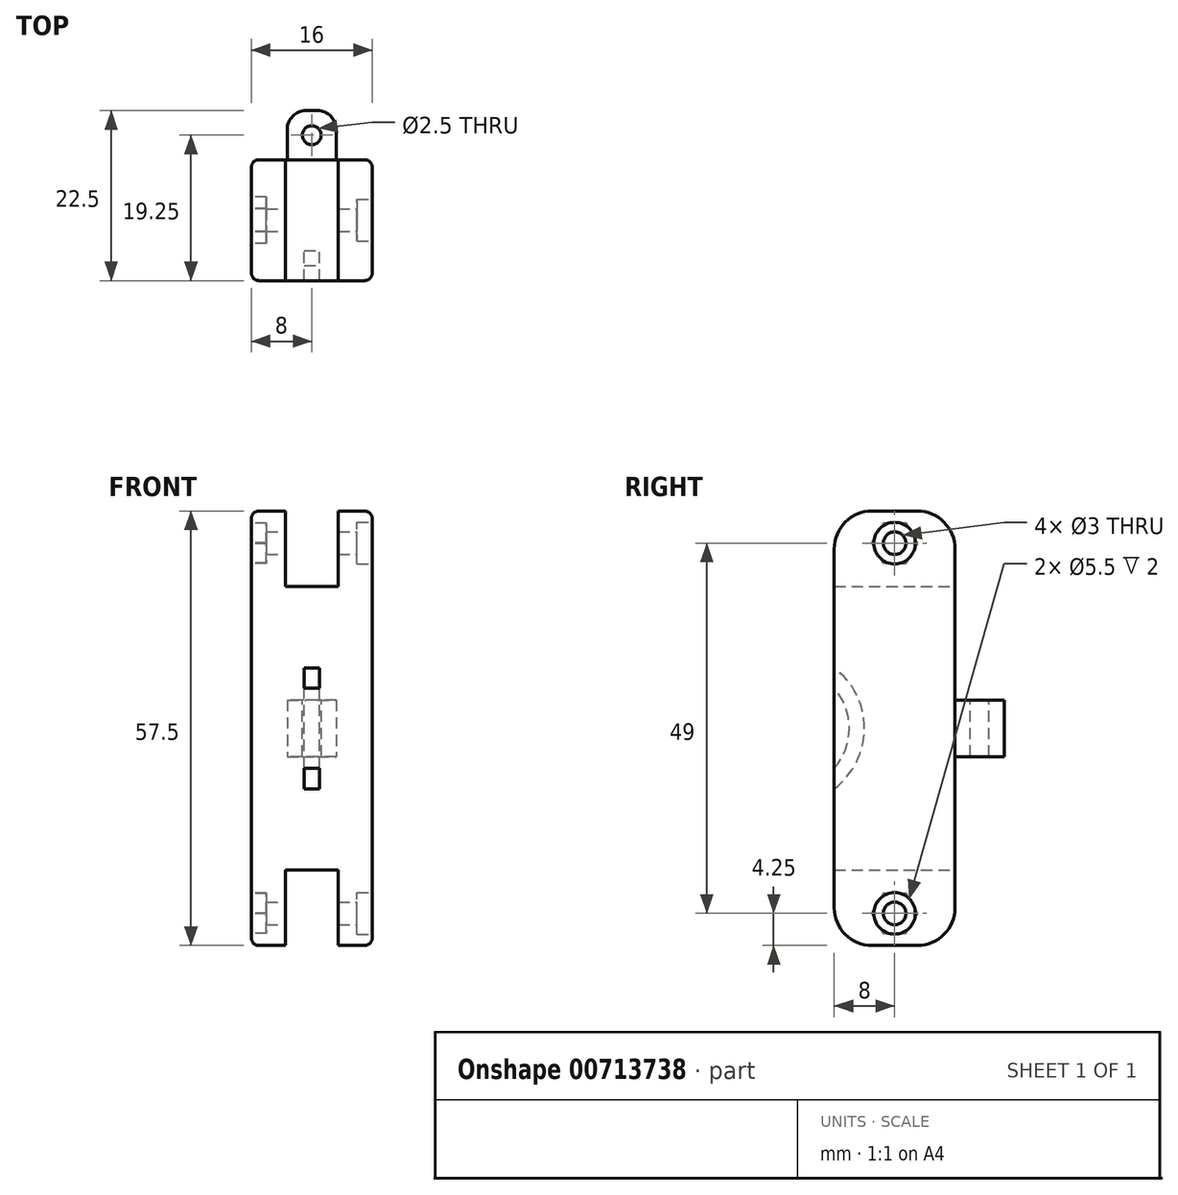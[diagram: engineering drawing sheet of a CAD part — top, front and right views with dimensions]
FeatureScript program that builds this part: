
annotation { "Feature Type Name" : "Feature", "Feature Type Description" : "" }
export const myFeature = defineFeature(function(context is Context, id is Id, definition is map)
    precondition{}
    {
        {
            var Q0;
            Q0=qCreatedBy(makeId("Front.planeOp"),FACE);
            var sketch = newSketch(context, id + "F0", { "sketchPlane" : qUnion([Q0])});
            skLineSegment(sketch, "E0.bottom", {"start": v(8, -28.75) * mm, "end": v(-8, -28.75) * mm});
            skLineSegment(sketch, "E0.top", {"start": v(8, 28.75) * mm, "end": v(-8, 28.75) * mm});
            skLineSegment(sketch, "E0.left", {"start": v(8, -28.75) * mm, "end": v(8, 28.75) * mm});
            skLineSegment(sketch, "E0.right", {"start": v(-8, -28.75) * mm, "end": v(-8, 28.75) * mm});
            skPoint(sketch, "E0.middle", {"position": v(0, 0) * mm});
            skLineSegment(sketch, "E1.top", {"start": v(-3.5, -18.75) * mm, "end": v(3.5, -18.75) * mm});
            skLineSegment(sketch, "E1.left", {"start": v(-3.5, -28.75) * mm, "end": v(-3.5, -18.75) * mm});
            skLineSegment(sketch, "E1.right", {"start": v(3.5, -28.75) * mm, "end": v(3.5, -18.75) * mm});
            skLineSegment(sketch, "E2.bottom", {"start": v(-3.5, 28.75) * mm, "end": v(3.5, 28.75) * mm});
            skLineSegment(sketch, "E2.top", {"start": v(-3.5, 18.75) * mm, "end": v(3.5, 18.75) * mm});
            skLineSegment(sketch, "E2.left", {"start": v(-3.5, 28.75) * mm, "end": v(-3.5, 18.75) * mm});
            skLineSegment(sketch, "E2.right", {"start": v(3.5, 28.75) * mm, "end": v(3.5, 18.75) * mm});
            skPoint(sketch, "E3", {"position": v(0, 23) * mm});
            skPoint(sketch, "E4", {"position": v(0, -26) * mm});
            skPoint(sketch, "E5", {"position": v(0, 18.75) * mm});
            skLineSegment(sketch, "E6", {"start": v(-3.5, -28.75) * mm, "end": v(3.5, -28.75) * mm});
            skLineSegment(sketch, "E7.bottom", {"start": v(3.25, 3.75) * mm, "end": v(-3.25, 3.75) * mm});
            skLineSegment(sketch, "E7.top", {"start": v(3.25, -3.75) * mm, "end": v(-3.25, -3.75) * mm});
            skLineSegment(sketch, "E7.left", {"start": v(3.25, 3.75) * mm, "end": v(3.25, -3.75) * mm});
            skLineSegment(sketch, "E7.right", {"start": v(-3.25, 3.75) * mm, "end": v(-3.25, -3.75) * mm});
            skSolve(sketch);
        }
        {
            var Q0;
            {var subQ1=sQuery(id+"F0.wireOp",EDGE,"E0.left");Q0=makeQuery(id+"F0.imprint","IMPRINT",FACE,{"disambiguationData":[TD([[makeQuery(id+"F0.imprint","IMPRINT",EDGE,{"derivedFrom":subQ1}),1.0]])]});}
            extrude(context, id + "F1", {"entities" : qUnion([Q0]), "endBound" : BoundingType.SYMMETRIC, "depth" : 16 * mm});
        }
        {
            var Q0;
            Q0=makeQuery(id+"F1.opExtrude","SWEPT_FACE",FACE,{"disambiguationData":[OSD([sQuery(id+"F0.wireOp",EDGE,"E0.left")])]});
            var sketch = newSketch(context, id + "F2", { "sketchPlane" : qUnion([Q0])});
            skLineSegment(sketch, "E8", {"start": v(0, 28.75) * mm, "end": v(0, 24.5) * mm});
            skPoint(sketch, "E8.endSnap0", {"position": v(0, 28.75) * mm});
            skLineSegment(sketch, "E9", {"start": v(0, -28.75) * mm, "end": v(0, -24.5) * mm});
            skPoint(sketch, "E9.endSnap0", {"position": v(0, -28.75) * mm});
            skCircle(sketch, "E10", {"center": v(0, 24.5) * mm, "radius": 2.75 * mm});
            skCircle(sketch, "E11", {"center": v(0, -24.5) * mm, "radius": 2.75 * mm});
            skCircle(sketch, "E12", {"center": v(0, 24.5) * mm, "radius": 1.5 * mm});
            skCircle(sketch, "E13", {"center": v(0, -24.5) * mm, "radius": 1.5 * mm});
            skSolve(sketch);
        }
        {
            var Q0;
            Q0=makeQuery(id+"F2.imprint","IMPRINT",FACE,{"disambiguationData":[TD([[makeQuery(id+"F2.imprint","IMPRINT",EDGE,{"derivedFrom":sQuery(id+"F2.wireOp",EDGE,"E10")}),1.0]])]});
            var Q1;
            Q1=makeQuery(id+"F2.imprint","IMPRINT",FACE,{"disambiguationData":[TD([[makeQuery(id+"F2.imprint","IMPRINT",EDGE,{"derivedFrom":sQuery(id+"F2.wireOp",EDGE,"E11")}),1.0]])]});
            extrude(context, id + "F3", {"entities" : qUnion([Q0, Q1]), "operationType" : NewBodyOperationType.REMOVE, "oppositeDirection" : true, "depth" : 2 * mm});
        }
        {
            var Q0;
            Q0=makeQuery(id+"F3.boolean.opBoolean","SPLIT",FACE,{"disambiguationData":[TD([makeQuery(id+"F3.opExtrude","SWEPT_FACE",FACE,{"disambiguationData":[OSD([sQuery(id+"F2.wireOp",EDGE,"E12")])]})])],"derivedFrom":makeQuery(id+"F1.opExtrude","SWEPT_FACE",FACE,{"disambiguationData":[OSD([sQuery(id+"F0.wireOp",EDGE,"E0.left")])]})});
            var Q1;
            Q1=makeQuery(id+"F3.boolean.opBoolean","SPLIT",FACE,{"disambiguationData":[TD([makeQuery(id+"F3.opExtrude","SWEPT_FACE",FACE,{"disambiguationData":[OSD([sQuery(id+"F2.wireOp",EDGE,"E13")])]})])],"derivedFrom":makeQuery(id+"F1.opExtrude","SWEPT_FACE",FACE,{"disambiguationData":[OSD([sQuery(id+"F0.wireOp",EDGE,"E0.left")])]})});
            extrude(context, id + "F4", {"entities" : qUnion([Q0, Q1]), "operationType" : NewBodyOperationType.REMOVE, "oppositeDirection" : true, "depth" : 25 * mm});
        }
        {
            var Q0;
            Q0=makeQuery(id+"F1.opExtrude","SWEPT_FACE",FACE,{"disambiguationData":[OSD([sQuery(id+"F0.wireOp",EDGE,"E0.right")])]});
            var sketch = newSketch(context, id + "F5", { "sketchPlane" : qUnion([Q0])});
            skLineSegment(sketch, "E14", {"start": v(0, 28.75) * mm, "end": v(0, 24.5) * mm});
            skLineSegment(sketch, "E15", {"start": v(0, -28.75) * mm, "end": v(0, -24.5) * mm});
            skCircle(sketch, "E16.cCircle", {"center": v(0, 24.5) * mm, "radius": 2.65 * mm, "construction": true});
            skLineSegment(sketch, "E16.0", {"start": v(3.06, 24.55) * mm, "end": v(1.57, 21.88) * mm});
            skLineSegment(sketch, "E16.1", {"start": v(1.57, 21.88) * mm, "end": v(-1.49, 21.83) * mm});
            skLineSegment(sketch, "E16.2", {"start": v(-1.49, 21.83) * mm, "end": v(-3.06, 24.45) * mm});
            skLineSegment(sketch, "E16.3", {"start": v(-3.06, 24.45) * mm, "end": v(-1.57, 27.12) * mm});
            skLineSegment(sketch, "E16.4", {"start": v(-1.57, 27.12) * mm, "end": v(1.49, 27.17) * mm});
            skLineSegment(sketch, "E16.5", {"start": v(1.49, 27.17) * mm, "end": v(3.06, 24.55) * mm});
            skPoint(sketch, "E16.0.midPoint", {"position": v(2.32, 23.21) * mm});
            skCircle(sketch, "E17.cCircle", {"center": v(0, -24.5) * mm, "radius": 2.65 * mm, "construction": true});
            skLineSegment(sketch, "E17.0", {"start": v(1.5, -21.83) * mm, "end": v(3.06, -24.46) * mm});
            skLineSegment(sketch, "E17.1", {"start": v(3.06, -24.46) * mm, "end": v(1.56, -27.13) * mm});
            skLineSegment(sketch, "E17.2", {"start": v(1.56, -27.13) * mm, "end": v(-1.5, -27.17) * mm});
            skLineSegment(sketch, "E17.3", {"start": v(-1.5, -27.17) * mm, "end": v(-3.06, -24.54) * mm});
            skLineSegment(sketch, "E17.4", {"start": v(-3.06, -24.54) * mm, "end": v(-1.56, -21.87) * mm});
            skLineSegment(sketch, "E17.5", {"start": v(-1.56, -21.87) * mm, "end": v(1.5, -21.83) * mm});
            skPoint(sketch, "E17.0.midPoint", {"position": v(2.28, -23.15) * mm});
            skSolve(sketch);
        }
        {
            var Q0;
            {var subQ0=sQuery(id+"F5.wireOp",EDGE,"E16.0");Q0=makeQuery(id+"F5.imprint","IMPRINT",FACE,{"disambiguationData":[TD([[makeQuery(id+"F5.imprint","IMPRINT",EDGE,{"derivedFrom":subQ0}),-1.0]])]});}
            var Q1;
            Q1=makeQuery(id+"F5.imprint","IMPRINT",FACE,{"disambiguationData":[TD([[makeQuery(id+"F5.imprint","IMPRINT",EDGE,{"derivedFrom":sQuery(id+"F5.wireOp",EDGE,"E17.0")}),-1.0]])]});
            extrude(context, id + "F6", {"entities" : qUnion([Q0, Q1]), "operationType" : NewBodyOperationType.REMOVE, "oppositeDirection" : true, "depth" : 2 * mm});
        }
        {
            var Q0;
            {var subQ0=sQuery(id+"F0.wireOp",EDGE,"E0.top");Q0=makeQuery(id+"F1.opExtrude","CAP_EDGE",EDGE,{"disambiguationData":[OSD([subQ0]),TDD([makeQuery(id+"F0.imprint","IMPRINT",EDGE,{"disambiguationData":[TD([[makeQuery(id+"F0.imprint","INTERSECT",VERTEX,{"derivedFrom":[subQ0,sQuery(id+"F0.wireOp",EDGE,"E0.left")]}),-1.0]])],"derivedFrom":subQ0})])],"isStart":false});}
            var Q1;
            {var subQ0=sQuery(id+"F0.wireOp",EDGE,"E0.top");Q1=makeQuery(id+"F1.opExtrude","CAP_EDGE",EDGE,{"disambiguationData":[OSD([subQ0]),TDD([makeQuery(id+"F0.imprint","IMPRINT",EDGE,{"disambiguationData":[TD([[makeQuery(id+"F0.imprint","INTERSECT",VERTEX,{"derivedFrom":[subQ0,sQuery(id+"F0.wireOp",EDGE,"E0.left")]}),-1.0]])],"derivedFrom":subQ0})])],"isStart":true});}
            var Q2;
            {var subQ0=sQuery(id+"F0.wireOp",EDGE,"E0.top");Q2=makeQuery(id+"F1.opExtrude","CAP_EDGE",EDGE,{"disambiguationData":[OSD([subQ0]),TDD([makeQuery(id+"F0.imprint","IMPRINT",EDGE,{"disambiguationData":[TD([[makeQuery(id+"F0.imprint","INTERSECT",VERTEX,{"derivedFrom":[subQ0,sQuery(id+"F0.wireOp",EDGE,"E0.right")]}),1.0]])],"derivedFrom":subQ0})])],"isStart":true});}
            var Q3;
            {var subQ0=sQuery(id+"F0.wireOp",EDGE,"E0.top");Q3=makeQuery(id+"F1.opExtrude","CAP_EDGE",EDGE,{"disambiguationData":[OSD([subQ0]),TDD([makeQuery(id+"F0.imprint","IMPRINT",EDGE,{"disambiguationData":[TD([[makeQuery(id+"F0.imprint","INTERSECT",VERTEX,{"derivedFrom":[subQ0,sQuery(id+"F0.wireOp",EDGE,"E0.right")]}),1.0]])],"derivedFrom":subQ0})])],"isStart":false});}
            fillet(context, id + "F7", {"entities" : qUnion([Q0, Q1, Q2, Q3]), "radius" : 5 * mm, "tangentPropagation" : true, "allowEdgeOverflow" : false});
        }
        {
            var Q0;
            {var subQ0=sQuery(id+"F0.wireOp",EDGE,"E0.bottom");Q0=makeQuery(id+"F1.opExtrude","CAP_EDGE",EDGE,{"disambiguationData":[OSD([subQ0]),TDD([makeQuery(id+"F0.imprint","IMPRINT",EDGE,{"disambiguationData":[TD([[makeQuery(id+"F0.imprint","INTERSECT",VERTEX,{"derivedFrom":[subQ0,sQuery(id+"F0.wireOp",EDGE,"E0.left")]}),-1.0]])],"derivedFrom":subQ0})])],"isStart":true});}
            var Q1;
            {var subQ0=sQuery(id+"F0.wireOp",EDGE,"E0.bottom");Q1=makeQuery(id+"F1.opExtrude","CAP_EDGE",EDGE,{"disambiguationData":[OSD([subQ0]),TDD([makeQuery(id+"F0.imprint","IMPRINT",EDGE,{"disambiguationData":[TD([[makeQuery(id+"F0.imprint","INTERSECT",VERTEX,{"derivedFrom":[subQ0,sQuery(id+"F0.wireOp",EDGE,"E0.right")]}),1.0]])],"derivedFrom":subQ0})])],"isStart":true});}
            var Q2;
            {var subQ0=sQuery(id+"F0.wireOp",EDGE,"E0.bottom");Q2=makeQuery(id+"F1.opExtrude","CAP_EDGE",EDGE,{"disambiguationData":[OSD([subQ0]),TDD([makeQuery(id+"F0.imprint","IMPRINT",EDGE,{"disambiguationData":[TD([[makeQuery(id+"F0.imprint","INTERSECT",VERTEX,{"derivedFrom":[subQ0,sQuery(id+"F0.wireOp",EDGE,"E0.left")]}),-1.0]])],"derivedFrom":subQ0})])],"isStart":false});}
            var Q3;
            {var subQ0=sQuery(id+"F0.wireOp",EDGE,"E0.bottom");Q3=makeQuery(id+"F1.opExtrude","CAP_EDGE",EDGE,{"disambiguationData":[OSD([subQ0]),TDD([makeQuery(id+"F0.imprint","IMPRINT",EDGE,{"disambiguationData":[TD([[makeQuery(id+"F0.imprint","INTERSECT",VERTEX,{"derivedFrom":[subQ0,sQuery(id+"F0.wireOp",EDGE,"E0.right")]}),1.0]])],"derivedFrom":subQ0})])],"isStart":false});}
            fillet(context, id + "F8", {"entities" : qUnion([Q0, Q1, Q2, Q3]), "radius" : 5 * mm, "tangentPropagation" : true, "allowEdgeOverflow" : false});
        }
        {
            var Q0;
            Q0=makeQuery(id+"F1.opExtrude","CAP_EDGE",EDGE,{"disambiguationData":[OSD([sQuery(id+"F0.wireOp",EDGE,"E0.right")])],"isStart":false});
            var Q1;
            Q1=makeQuery(id+"F1.opExtrude","CAP_EDGE",EDGE,{"disambiguationData":[OSD([sQuery(id+"F0.wireOp",EDGE,"E0.left")])],"isStart":false});
            var Q2;
            Q2=makeQuery(id+"F1.opExtrude","CAP_EDGE",EDGE,{"disambiguationData":[OSD([sQuery(id+"F0.wireOp",EDGE,"E0.left")])],"isStart":true});
            var Q3;
            Q3=makeQuery(id+"F1.opExtrude","CAP_EDGE",EDGE,{"disambiguationData":[OSD([sQuery(id+"F0.wireOp",EDGE,"E0.right")])],"isStart":true});
            fillet(context, id + "F9", {"entities" : qUnion([Q0, Q1, Q2, Q3]), "radius" : 1 * mm, "tangentPropagation" : true, "allowEdgeOverflow" : false});
        }
        {
            var Q0;
            Q0=makeQuery(id+"F0.imprint","IMPRINT",FACE,{"disambiguationData":[TD([[makeQuery(id+"F0.imprint","IMPRINT",EDGE,{"derivedFrom":sQuery(id+"F0.wireOp",EDGE,"E7.bottom")}),1.0]])]});
            extrude(context, id + "F10", {"entities" : qUnion([Q0]), "operationType" : NewBodyOperationType.ADD, "endBound" : BoundingType.SYMMETRIC, "depth" : 29 * mm});
        }
        {
            var Q0;
            {var subQ0=sQuery(id+"F0.wireOp",EDGE,"E7.right");var subQ1=sQuery(id+"F0.wireOp",EDGE,"E7.left");var subQ2=sQuery(id+"F0.wireOp",EDGE,"E7.top");var subQ3=sQuery(id+"F0.wireOp",EDGE,"E7.bottom");Q0=makeQuery(id+"F10.boolean.opBoolean","SPLIT",FACE,{"disambiguationData":[TD([makeQuery(id+"F10.opExtrude","CAP_FACE",FACE,{"disambiguationData":[OSD([subQ3,subQ2,subQ1,subQ0])],"isStart":true})])],"derivedFrom":makeQuery(id+"F10.opExtrude","SWEPT_FACE",FACE,{"disambiguationData":[OSD([subQ3])]})});}
            var sketch = newSketch(context, id + "F11", { "sketchPlane" : qUnion([Q0])});
            skPoint(sketch, "E18", {"position": v(0, 11.25) * mm});
            skCircle(sketch, "E19", {"center": v(0, 11.25) * mm, "radius": 1.25 * mm});
            skCircle(sketch, "E20", {"center": v(0, -11.25) * mm, "radius": 1.25 * mm});
            skSolve(sketch);
        }
        {
            var Q0;
            Q0=makeQuery(id+"F11.imprint","IMPRINT",FACE,{"disambiguationData":[TD([[makeQuery(id+"F11.imprint","IMPRINT",EDGE,{"derivedFrom":sQuery(id+"F11.wireOp",EDGE,"E19")}),1.0]])]});
            var Q1;
            Q1=makeQuery(id+"F11.imprint","IMPRINT",FACE,{"disambiguationData":[TD([[makeQuery(id+"F11.imprint","IMPRINT",EDGE,{"derivedFrom":sQuery(id+"F11.wireOp",EDGE,"E20")}),1.0]])]});
            extrude(context, id + "F12", {"entities" : qUnion([Q0, Q1]), "operationType" : NewBodyOperationType.REMOVE, "endBound" : BoundingType.THROUGH_ALL, "oppositeDirection" : true, "depth" : 25 * mm});
        }
        {
            var Q0;
            Q0=makeQuery(id+"F10.opExtrude","CAP_EDGE",EDGE,{"disambiguationData":[OSD([sQuery(id+"F0.wireOp",EDGE,"E7.right")])],"isStart":true});
            var Q1;
            Q1=makeQuery(id+"F10.opExtrude","CAP_EDGE",EDGE,{"disambiguationData":[OSD([sQuery(id+"F0.wireOp",EDGE,"E7.left")])],"isStart":true});
            var Q2;
            Q2=makeQuery(id+"F10.opExtrude","CAP_EDGE",EDGE,{"disambiguationData":[OSD([sQuery(id+"F0.wireOp",EDGE,"E7.right")])],"isStart":false});
            var Q3;
            Q3=makeQuery(id+"F10.opExtrude","CAP_EDGE",EDGE,{"disambiguationData":[OSD([sQuery(id+"F0.wireOp",EDGE,"E7.left")])],"isStart":false});
            fillet(context, id + "F13", {"entities" : qUnion([Q0, Q1, Q2, Q3]), "radius" : 2.5 * mm, "tangentPropagation" : true, "allowEdgeOverflow" : false});
        }
        {
            var Q0;
            {var subQ0=sQuery(id+"F0.wireOp",EDGE,"E7.right");var subQ1=sQuery(id+"F0.wireOp",EDGE,"E7.left");var subQ2=sQuery(id+"F0.wireOp",EDGE,"E7.top");var subQ3=sQuery(id+"F0.wireOp",EDGE,"E7.bottom");Q0=makeQuery(id+"F10.boolean.opBoolean","SPLIT",FACE,{"disambiguationData":[TD([makeQuery(id+"F10.opExtrude","CAP_FACE",FACE,{"disambiguationData":[OSD([subQ3,subQ2,subQ1,subQ0])],"isStart":false})])],"derivedFrom":makeQuery(id+"F10.opExtrude","SWEPT_FACE",FACE,{"disambiguationData":[OSD([subQ3])]})});}
            var sketch = newSketch(context, id + "F14", { "sketchPlane" : qUnion([Q0])});
            skLineSegment(sketch, "E21.0.0", {"start": v(-0.75, -14.5) * mm, "end": v(0.75, -14.5) * mm});
            skArc(sketch, "E21.0.1", {"start": v(0.75, -14.5) * mm, "mid": v(2.52, -13.77) * mm, "end": v(3.25, -12) * mm});
            skLineSegment(sketch, "E21.0.2", {"start": v(3.25, -12) * mm, "end": v(3.25, -8) * mm});
            skLineSegment(sketch, "E21.0.3", {"start": v(3.25, -8) * mm, "end": v(-3.25, -8) * mm});
            skLineSegment(sketch, "E21.0.4", {"start": v(-3.25, -8) * mm, "end": v(-3.25, -12) * mm});
            skArc(sketch, "E21.0.5", {"start": v(-3.25, -12) * mm, "mid": v(-2.52, -13.77) * mm, "end": v(-0.75, -14.5) * mm});
            skSolve(sketch);
        }
        {
            var Q0;
            Q0=makeQuery(id+"F14.imprint","IMPRINT",FACE,{"disambiguationData":[TD([[makeQuery(id+"F14.imprint","IMPRINT",EDGE,{"derivedFrom":sQuery(id+"F14.wireOp",EDGE,"E21.0.0")}),-1.0]])]});
            extrude(context, id + "F15", {"entities" : qUnion([Q0]), "operationType" : NewBodyOperationType.REMOVE, "endBound" : BoundingType.THROUGH_ALL, "oppositeDirection" : true, "depth" : 25 * mm});
        }
        {
            var Q0;
            Q0=qCreatedBy(makeId("Right.planeOp"),FACE);
            var sketch = newSketch(context, id + "F16", { "sketchPlane" : qUnion([Q0])});
            skLineSegment(sketch, "E22", {"start": v(-8, 18.75) * mm, "end": v(-8, 5.3) * mm});
            skArc(sketch, "E23", {"start": v(-8, -8) * mm, "mid": v(-4, 0) * mm, "end": v(-8, 8) * mm});
            skPoint(sketch, "E23.first.point", {"position": v(-8, -8) * mm});
            skPoint(sketch, "E23.second.point", {"position": v(-8, 8) * mm});
            skPoint(sketch, "E23.third.point", {"position": v(-24, 0) * mm});
            skArc(sketch, "E24", {"start": v(-8, -5.3) * mm, "mid": v(-6, 0) * mm, "end": v(-8, 5.3) * mm});
            skLineSegment(sketch, "E25", {"start": v(-8, 5.3) * mm, "end": v(-8, 8) * mm});
            skLineSegment(sketch, "E26", {"start": v(-8, -8) * mm, "end": v(-8, -5.3) * mm});
            skLineSegment(sketch, "E27.trimOffspring", {"start": v(-8, -5.3) * mm, "end": v(-8, -18.75) * mm});
            skSolve(sketch);
        }
        {
            var Q0;
            Q0=qSketchRegion(id+"F16",true);
            extrude(context, id + "F17", {"entities" : qUnion([Q0]), "operationType" : NewBodyOperationType.REMOVE, "endBound" : BoundingType.SYMMETRIC, "oppositeDirection" : true, "depth" : 2 * mm});
        }
    });
